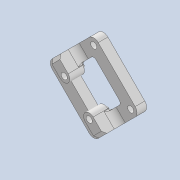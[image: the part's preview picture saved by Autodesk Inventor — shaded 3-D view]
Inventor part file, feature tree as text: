
AUTODESK INVENTOR PART (.ipt)
format: ipt  version: 2020 (Build 240168000, 168)  size: 330,752 bytes
history: native  units: mm
features: projected_geometry x11, sketch x8, extrude x6, other x6, thicken_offset x5, hole x2, chamfer x1, fillet x1, plane x1, reference x1
ambient origin geometry x8: Origin, YZ Plane, XZ Plane, XY Plane, X Axis, Y Axis, Z Axis, Center Point
bodies: Solid1 (feature_tree)
feature tree (42):
  extrude  "Extrusion1"  Depth=4.0mm
  extrude  "Extrusion2"  Depth=4.0mm
  extrude  "Extrusion3"  Depth=2.0mm
  thicken_offset  "Thicken1"
  thicken_offset  "Thicken2"
  thicken_offset  "Thicken3"
  thicken_offset  "Thicken4"
  chamfer  "Chamfer2"  Distance=6.3mm
  fillet  "Fillet5"  Radius=6.0mm
  hole  "Hole1"  [1 undecoded]
  hole  "Hole2"  [1 undecoded]
  plane  "Work Plane1"
  extrude  "Extrusion4"  Depth=1.5mm
  extrude  "Extrusion5"  Depth=1.5mm
  extrude  "Extrusion6"  Depth=1.5mm
  thicken_offset  "Thicken5"
  sketch  "Sketch1"  dims[d0=4.0mm d1=4.0mm]
  reference  "Reference1"
  sketch  "Sketch2"  dims[d2=4.0mm d3=4.0mm]
  projected_geometry  "Projected Loop1"
  sketch  "Sketch3"  dims[d4=2.0mm d5=0.0mm d6=5.5mm]
  projected_geometry  "Projected Loop2"
  projected_geometry  "Projected Loop3"
  projected_geometry  "Projected Loop4"
  sketch  "Sketch4"  dims[d7=4.0mm]
  projected_geometry  "Projected Loop5"
  projected_geometry  "Projected Loop6"
  sketch  "Sketch5"  dims[d8=4.0mm]
  projected_geometry  "Projected Loop7"
  projected_geometry  "Projected Loop8"
  sketch  "Sketch6"  dims[d9=4.0mm d10=6.3mm d11=0.0mm d12=6.0mm]
  sketch  "Sketch7"  dims[d13=4.0mm d14=6.0mm]
  projected_geometry  "Projected Loop9"
  projected_geometry  "Projected Loop10"
  sketch  "Sketch8"  dims[d15=4.0mm d16=6.0mm d17=0.0mm d21=0.25mm d22=0.25mm d23=0.25mm d24=0.25mm d27=1.0mm d28=1.0mm d29=1.0mm d30=1.0mm d33=1.0mm d34=2.0mm d35=45.0deg d36=1.0mm d37=1.9mm d38=6.0mm d39=4.0mm d40=2.0mm d41=90.0deg d42=4.0mm d43=0.0mm d44=1.9mm d45=6.0mm d46=4.0mm d47=2.0mm d48=90.0deg d49=4.0mm d50=0.0mm d51=6.0mm d52=6.0mm d53=6.0mm d54=6.0mm d55=35.0mm d56=3.5mm d57=35.0mm d58=3.5mm d59=6.3mm d60=0.0mm d61=6.3mm d62=0.0mm d63=1.9mm d64=1.9mm d65=6.3mm d66=0.0mm d69=1.5mm d70=1.5mm d18=0.5mm d19=0.872665mm]
  projected_geometry  "Projected Loop11"
  parser-record x2  (decoder bookkeeping rows leaked as tree rows — omitted from the tree; the rows remain in map.json)
  other  "mot_27_ass.iam"
  other  "mot_27_2:1"
  other  "tip_3_ass_base.iam"
  other  "ext_shell_2:1"
note: 2 required parameter values undecoded (feature->parameter linkage not recoverable at this tier; creation-order binding heuristic only, values carry confidence <= 0.55)
note: 2 file-system paths scrubbed to <path> (originals preserved in map.json)
